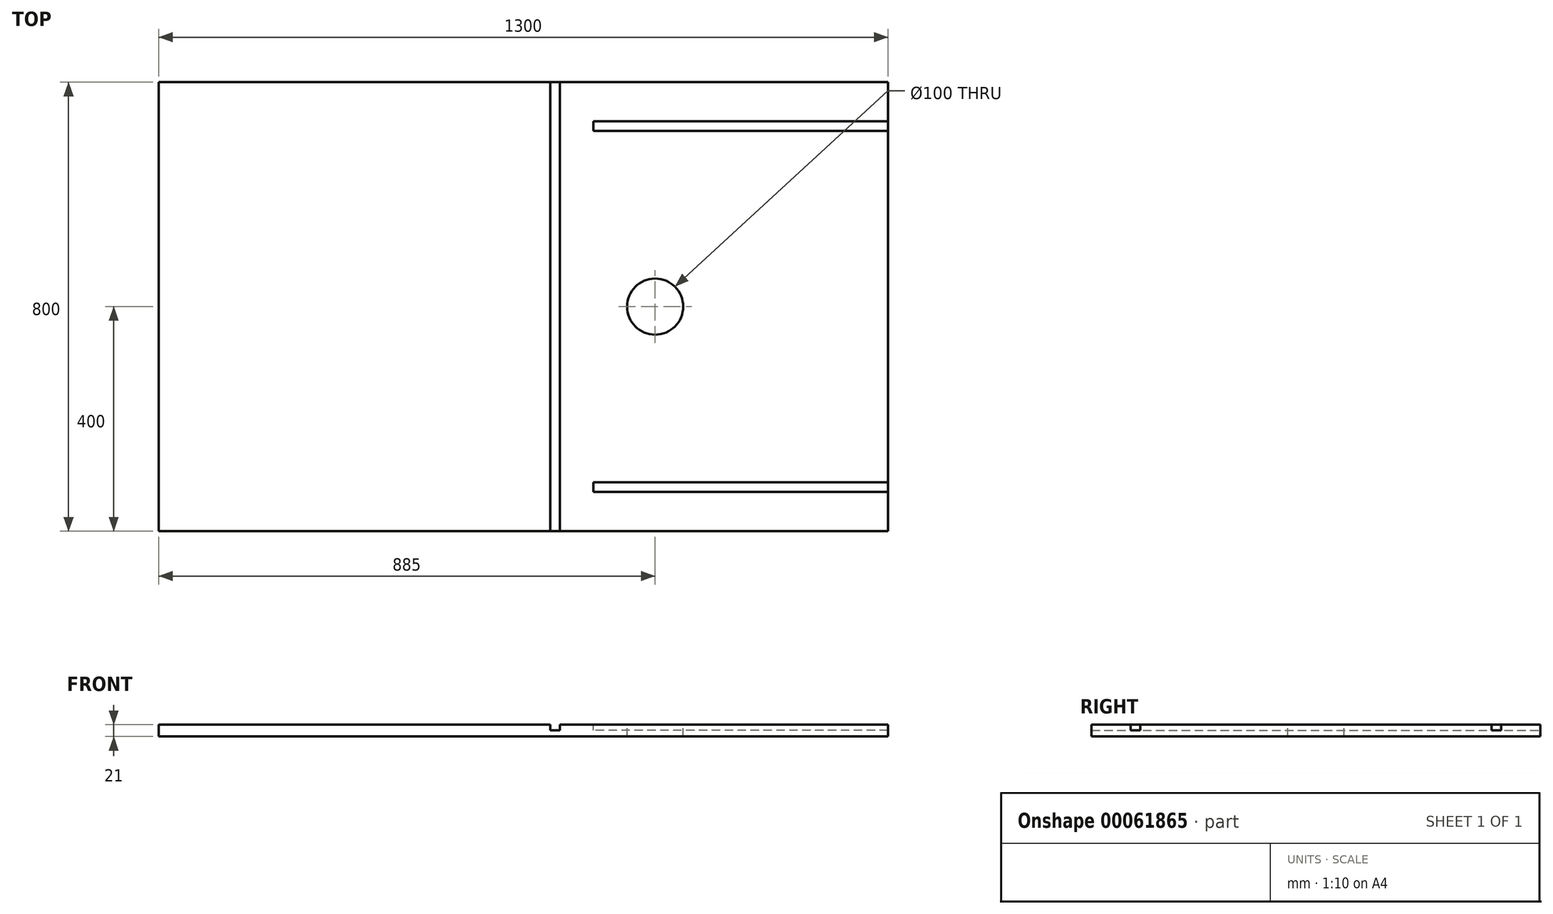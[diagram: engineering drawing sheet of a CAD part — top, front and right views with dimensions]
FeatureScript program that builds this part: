
annotation { "Feature Type Name" : "Feature", "Feature Type Description" : "" }
export const myFeature = defineFeature(function(context is Context, id is Id, definition is map)
    precondition{}
    {
        {
            var Q0;
            Q0=qCreatedBy(makeId("Top.planeOp"),FACE);
            var sketch = newSketch(context, id + "F0", { "sketchPlane" : qUnion([Q0])});
            skLineSegment(sketch, "E0.bottom", {"start": v(0, 0) * mm, "end": v(1300, 0) * mm});
            skLineSegment(sketch, "E0.top", {"start": v(0, 800) * mm, "end": v(1300, 800) * mm});
            skLineSegment(sketch, "E0.left", {"start": v(0, 0) * mm, "end": v(0, 800) * mm});
            skLineSegment(sketch, "E0.right", {"start": v(1300, 0) * mm, "end": v(1300, 800) * mm});
            skSolve(sketch);
        }
        {
            var Q0;
            Q0 = qSketchRegion(id + "F0", true);
            extrude(context, id + "F1", {"entities" : qUnion([Q0]), "depth" : 21 * mm});
        }
        {
            var Q0;
            Q0=makeQuery(id+"F1.opExtrude","CAP_FACE",FACE,{"disambiguationData":[OSD([sQuery(id+"F0.wireOp",EDGE,"E0.bottom"),sQuery(id+"F0.wireOp",EDGE,"E0.top"),sQuery(id+"F0.wireOp",EDGE,"E0.left"),sQuery(id+"F0.wireOp",EDGE,"E0.right")])],"isStart":false});
            var sketch = newSketch(context, id + "F2", { "sketchPlane" : qUnion([Q0])});
            skLineSegment(sketch, "E1.0", {"start": v(1300, 0) * mm, "end": v(1300, 800) * mm, "construction": true});
            skLineSegment(sketch, "E2.bottom", {"start": v(715, 0) * mm, "end": v(698, 0) * mm});
            skLineSegment(sketch, "E2.top", {"start": v(715, 800) * mm, "end": v(698, 800) * mm});
            skLineSegment(sketch, "E2.left", {"start": v(715, 0) * mm, "end": v(715, 800) * mm});
            skLineSegment(sketch, "E2.right", {"start": v(698, 0) * mm, "end": v(698, 800) * mm});
            skLineSegment(sketch, "E3.bottom", {"start": v(1300, 70) * mm, "end": v(775, 70) * mm});
            skLineSegment(sketch, "E3.top", {"start": v(1300, 87) * mm, "end": v(775, 87) * mm});
            skLineSegment(sketch, "E3.left", {"start": v(1300, 70) * mm, "end": v(1300, 87) * mm});
            skLineSegment(sketch, "E3.right", {"start": v(775, 70) * mm, "end": v(775, 87) * mm});
            skLineSegment(sketch, "E4.bottom", {"start": v(1300, 713) * mm, "end": v(775, 713) * mm});
            skLineSegment(sketch, "E4.top", {"start": v(1300, 730) * mm, "end": v(775, 730) * mm});
            skLineSegment(sketch, "E4.left", {"start": v(1300, 713) * mm, "end": v(1300, 730) * mm});
            skLineSegment(sketch, "E4.right", {"start": v(775, 713) * mm, "end": v(775, 730) * mm});
            skLineSegment(sketch, "E5", {"start": v(775, 721.5) * mm, "end": v(1300, 721.5) * mm, "construction": true});
            skLineSegment(sketch, "E6", {"start": v(775, 78.5) * mm, "end": v(1300, 78.5) * mm, "construction": true});
            skSolve(sketch);
        }
        {
            var Q0;
            Q0=makeQuery(id+"F2.imprint","IMPRINT",FACE,{"disambiguationData":[TD([[makeQuery(id+"F2.imprint","IMPRINT",EDGE,{"derivedFrom":sQuery(id+"F2.wireOp",EDGE,"E2.bottom")}),1.0]])]});
            var Q1;
            Q1=makeQuery(id+"F2.imprint","IMPRINT",FACE,{"disambiguationData":[TD([[makeQuery(id+"F2.imprint","IMPRINT",EDGE,{"derivedFrom":sQuery(id+"F2.wireOp",EDGE,"E4.bottom")}),-1.0]])]});
            var Q2;
            Q2=makeQuery(id+"F2.imprint","IMPRINT",FACE,{"disambiguationData":[TD([[makeQuery(id+"F2.imprint","IMPRINT",EDGE,{"derivedFrom":sQuery(id+"F2.wireOp",EDGE,"E3.bottom")}),-1.0]])]});
            extrude(context, id + "F3", {"entities" : qUnion([Q0, Q1, Q2]), "operationType" : NewBodyOperationType.REMOVE, "oppositeDirection" : true, "depth" : 10.2 * mm});
        }
        {
            var Q0;
            {var subQ0=sQuery(id+"F0.wireOp",EDGE,"E0.right");var subQ1=sQuery(id+"F0.wireOp",EDGE,"E0.top");var subQ2=sQuery(id+"F0.wireOp",EDGE,"E0.bottom");Q0=makeQuery(id+"F3.boolean.opBoolean","SPLIT",FACE,{"disambiguationData":[TD([makeQuery(id+"F1.opExtrude","SWEPT_FACE",FACE,{"disambiguationData":[OSD([subQ0])]})])],"derivedFrom":makeQuery(id+"F1.opExtrude","CAP_FACE",FACE,{"disambiguationData":[OSD([subQ2,subQ1,sQuery(id+"F0.wireOp",EDGE,"E0.left"),subQ0])],"isStart":false})});}
            var sketch = newSketch(context, id + "F4", { "sketchPlane" : qUnion([Q0])});
            skLineSegment(sketch, "E7", {"start": v(1300, 400) * mm, "end": v(885, 400) * mm, "construction": true});
            skCircle(sketch, "E8", {"center": v(885, 400) * mm, "radius": 50 * mm});
            skSolve(sketch);
        }
        {
            var Q0;
            Q0=makeQuery(id+"F4.imprint","IMPRINT",FACE,{"disambiguationData":[TD([[makeQuery(id+"F4.imprint","IMPRINT",EDGE,{"derivedFrom":sQuery(id+"F4.wireOp",EDGE,"E8")}),1.0]])]});
            extrude(context, id + "F5", {"entities" : qUnion([Q0]), "operationType" : NewBodyOperationType.REMOVE, "oppositeDirection" : true, "depth" : 25 * mm});
        }
    });
